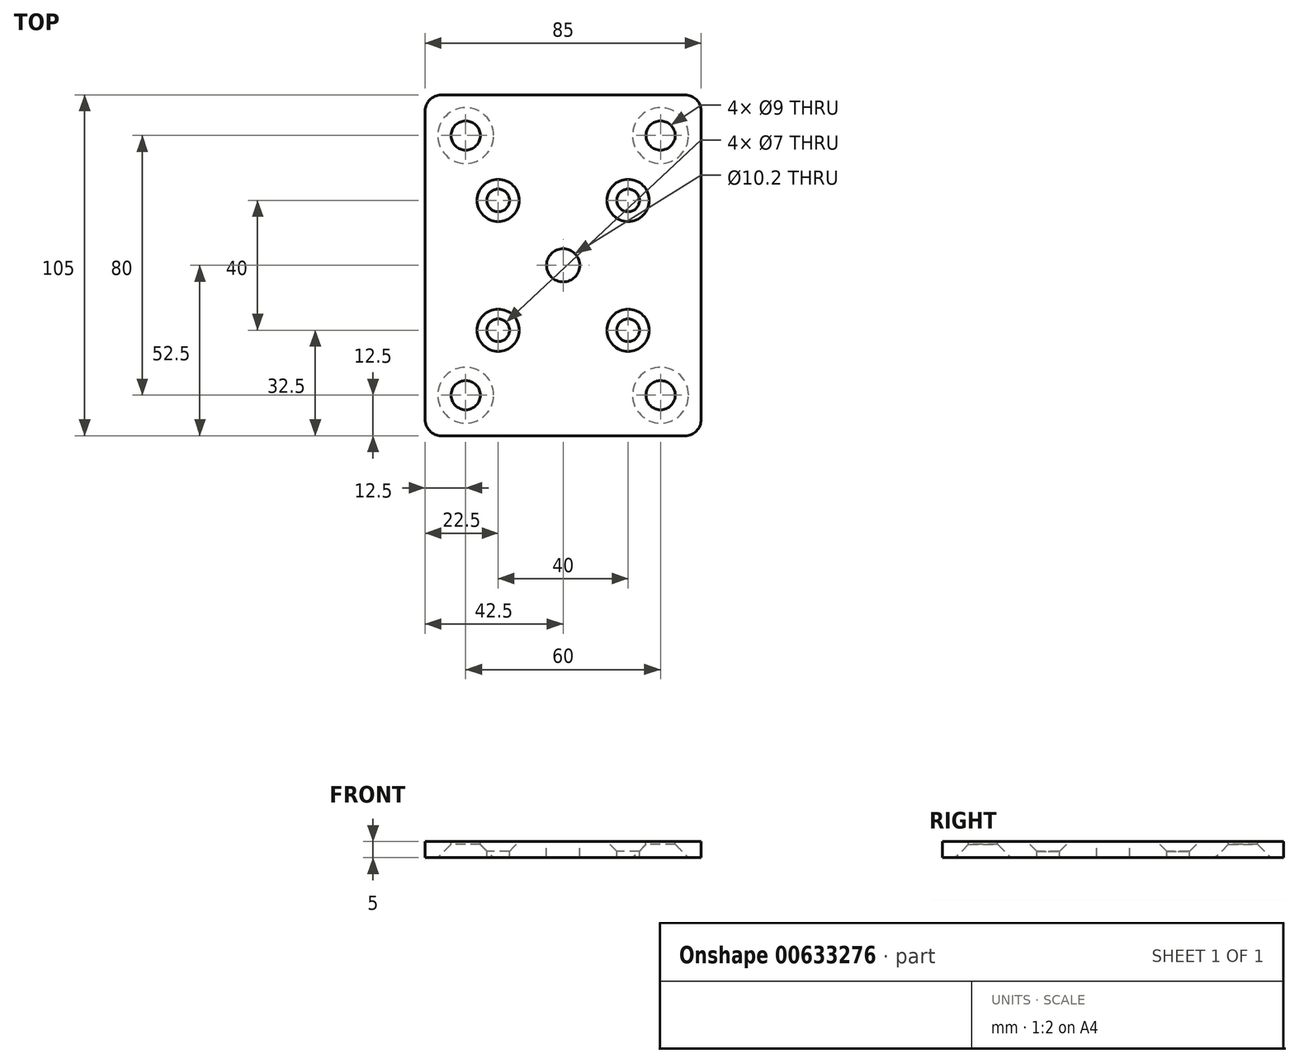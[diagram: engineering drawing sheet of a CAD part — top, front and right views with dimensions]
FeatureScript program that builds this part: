
annotation { "Feature Type Name" : "Feature", "Feature Type Description" : "" }
export const myFeature = defineFeature(function(context is Context, id is Id, definition is map)
    precondition{}
    {
        {
            var Q0;
            Q0=qCreatedBy(makeId("Top.planeOp"),FACE);
            var sketch = newSketch(context, id + "F0", { "sketchPlane" : qUnion([Q0])});
            skLineSegment(sketch, "E0.bottom", {"start": v(42.5, -52.5) * mm, "end": v(-42.5, -52.5) * mm});
            skLineSegment(sketch, "E0.top", {"start": v(42.5, 52.5) * mm, "end": v(-42.5, 52.5) * mm});
            skLineSegment(sketch, "E0.left", {"start": v(42.5, -52.5) * mm, "end": v(42.5, 52.5) * mm});
            skLineSegment(sketch, "E0.right", {"start": v(-42.5, -52.5) * mm, "end": v(-42.5, 52.5) * mm});
            skPoint(sketch, "E0.middle", {"position": v(0, 0) * mm});
            skSolve(sketch);
        }
        {
            var Q0;
            Q0=qSketchRegion(id+"F0",true);
            extrude(context, id + "F1", {"entities" : qUnion([Q0]), "oppositeDirection" : true, "depth" : 5 * mm});
        }
        {
            var Q0;
            Q0=makeQuery(id+"F1.opExtrude","CAP_FACE",FACE,{"disambiguationData":[OSD([sQuery(id+"F0.wireOp",EDGE,"E0.bottom"),sQuery(id+"F0.wireOp",EDGE,"E0.top"),sQuery(id+"F0.wireOp",EDGE,"E0.left"),sQuery(id+"F0.wireOp",EDGE,"E0.right")])],"isStart":true});
            var sketch = newSketch(context, id + "F2", { "sketchPlane" : qUnion([Q0])});
            skCircle(sketch, "E1", {"center": v(0, 0) * mm, "radius": 5.1 * mm});
            skCircle(sketch, "E2", {"center": v(30, 40) * mm, "radius": 4.5 * mm});
            skCircle(sketch, "E3", {"center": v(-30, 40) * mm, "radius": 4.5 * mm});
            skCircle(sketch, "E4", {"center": v(-30, -40) * mm, "radius": 4.5 * mm});
            skCircle(sketch, "E5", {"center": v(30, -40) * mm, "radius": 4.5 * mm});
            skSolve(sketch);
        }
        {
            var Q0;
            Q0=qSketchRegion(id+"F2",true);
            extrude(context, id + "F3", {"entities" : qUnion([Q0]), "operationType" : NewBodyOperationType.REMOVE, "endBound" : BoundingType.THROUGH_ALL, "oppositeDirection" : true, "depth" : 25 * mm});
        }
        {
            var Q0;
            Q0=makeQuery(id+"F1.opExtrude","CAP_FACE",FACE,{"disambiguationData":[OSD([sQuery(id+"F0.wireOp",EDGE,"E0.bottom"),sQuery(id+"F0.wireOp",EDGE,"E0.top"),sQuery(id+"F0.wireOp",EDGE,"E0.left"),sQuery(id+"F0.wireOp",EDGE,"E0.right")])],"isStart":true});
            var sketch = newSketch(context, id + "F4", { "sketchPlane" : qUnion([Q0])});
            skPoint(sketch, "E6", {"position": v(-20, 20) * mm});
            skPoint(sketch, "E7", {"position": v(20, 20) * mm});
            skPoint(sketch, "E8", {"position": v(20, -20) * mm});
            skPoint(sketch, "E9", {"position": v(-20, -20) * mm});
            skSolve(sketch);
        }
        {
            var Q0;
            Q0=sQuery(id+"F4.wireOp",VERTEX,"E6");
            var Q1;
            Q1=sQuery(id+"F4.wireOp",VERTEX,"E7");
            var Q2;
            Q2=sQuery(id+"F4.wireOp",VERTEX,"E8");
            var Q3;
            Q3=sQuery(id+"F4.wireOp",VERTEX,"E9");
            var Q4;
            Q4=makeQuery(id+"F1.opExtrude","SWEPT_BODY",BODY,{"disambiguationData":[OSD([sQuery(id+"F0.wireOp",EDGE,"E0.bottom"),sQuery(id+"F0.wireOp",EDGE,"E0.top"),sQuery(id+"F0.wireOp",EDGE,"E0.left"),sQuery(id+"F0.wireOp",EDGE,"E0.right")])]});
            hole(context, id + "F5", {"style" : HoleStyle.C_SINK, "endStyle" : HoleEndStyle.THROUGH, "holeDiameter" : 7 * mm, "cSinkDiameter" : 13 * mm, "cSinkAngle" : 90 * degree, "locations" : qUnion([Q0, Q1, Q2, Q3]), "scope" : qUnion([Q4]), "isTappedThrough" : true});
        }
        {
            var Q0;
            Q0=makeQuery(id+"F1.opExtrude","SWEPT_EDGE",EDGE,{"disambiguationData":[OSD([sQuery(id+"F0.wireOp",EDGE,"E0.bottom"),sQuery(id+"F0.wireOp",EDGE,"E0.right")])]});
            var Q1;
            Q1=makeQuery(id+"F1.opExtrude","SWEPT_EDGE",EDGE,{"disambiguationData":[OSD([sQuery(id+"F0.wireOp",EDGE,"E0.bottom"),sQuery(id+"F0.wireOp",EDGE,"E0.left")])]});
            var Q2;
            Q2=makeQuery(id+"F1.opExtrude","SWEPT_EDGE",EDGE,{"disambiguationData":[OSD([sQuery(id+"F0.wireOp",EDGE,"E0.top"),sQuery(id+"F0.wireOp",EDGE,"E0.left")])]});
            var Q3;
            Q3=makeQuery(id+"F1.opExtrude","SWEPT_EDGE",EDGE,{"disambiguationData":[OSD([sQuery(id+"F0.wireOp",EDGE,"E0.top"),sQuery(id+"F0.wireOp",EDGE,"E0.right")])]});
            fillet(context, id + "F6", {"entities" : qUnion([Q0, Q1, Q2, Q3]), "radius" : 5 * mm, "tangentPropagation" : true, "allowEdgeOverflow" : false});
        }
        {
            var Q0;
            Q0=makeQuery(id+"F3.boolean.opBoolean","INTERSECT",EDGE,{"derivedFrom":[makeQuery(id+"F1.opExtrude","CAP_FACE",FACE,{"disambiguationData":[OSD([sQuery(id+"F0.wireOp",EDGE,"E0.bottom"),sQuery(id+"F0.wireOp",EDGE,"E0.top"),sQuery(id+"F0.wireOp",EDGE,"E0.left"),sQuery(id+"F0.wireOp",EDGE,"E0.right")])],"isStart":false}),makeQuery(id+"F3.opExtrude","SWEPT_FACE",FACE,{"disambiguationData":[OSD([sQuery(id+"F2.wireOp",EDGE,"E2")])]})]});
            var Q1;
            Q1=makeQuery(id+"F3.boolean.opBoolean","INTERSECT",EDGE,{"derivedFrom":[makeQuery(id+"F1.opExtrude","CAP_FACE",FACE,{"disambiguationData":[OSD([sQuery(id+"F0.wireOp",EDGE,"E0.bottom"),sQuery(id+"F0.wireOp",EDGE,"E0.top"),sQuery(id+"F0.wireOp",EDGE,"E0.left"),sQuery(id+"F0.wireOp",EDGE,"E0.right")])],"isStart":false}),makeQuery(id+"F3.opExtrude","SWEPT_FACE",FACE,{"disambiguationData":[OSD([sQuery(id+"F2.wireOp",EDGE,"E3")])]})]});
            var Q2;
            Q2=makeQuery(id+"F3.boolean.opBoolean","INTERSECT",EDGE,{"derivedFrom":[makeQuery(id+"F1.opExtrude","CAP_FACE",FACE,{"disambiguationData":[OSD([sQuery(id+"F0.wireOp",EDGE,"E0.bottom"),sQuery(id+"F0.wireOp",EDGE,"E0.top"),sQuery(id+"F0.wireOp",EDGE,"E0.left"),sQuery(id+"F0.wireOp",EDGE,"E0.right")])],"isStart":false}),makeQuery(id+"F3.opExtrude","SWEPT_FACE",FACE,{"disambiguationData":[OSD([sQuery(id+"F2.wireOp",EDGE,"E4")])]})]});
            var Q3;
            Q3=makeQuery(id+"F3.boolean.opBoolean","INTERSECT",EDGE,{"derivedFrom":[makeQuery(id+"F1.opExtrude","CAP_FACE",FACE,{"disambiguationData":[OSD([sQuery(id+"F0.wireOp",EDGE,"E0.bottom"),sQuery(id+"F0.wireOp",EDGE,"E0.top"),sQuery(id+"F0.wireOp",EDGE,"E0.left"),sQuery(id+"F0.wireOp",EDGE,"E0.right")])],"isStart":false}),makeQuery(id+"F3.opExtrude","SWEPT_FACE",FACE,{"disambiguationData":[OSD([sQuery(id+"F2.wireOp",EDGE,"E5")])]})]});
            chamfer(context, id + "F7", {"entities" : qUnion([Q0, Q1, Q2, Q3]), "width" : 4.1 * mm, "tangentPropagation" : true});
        }
    });
